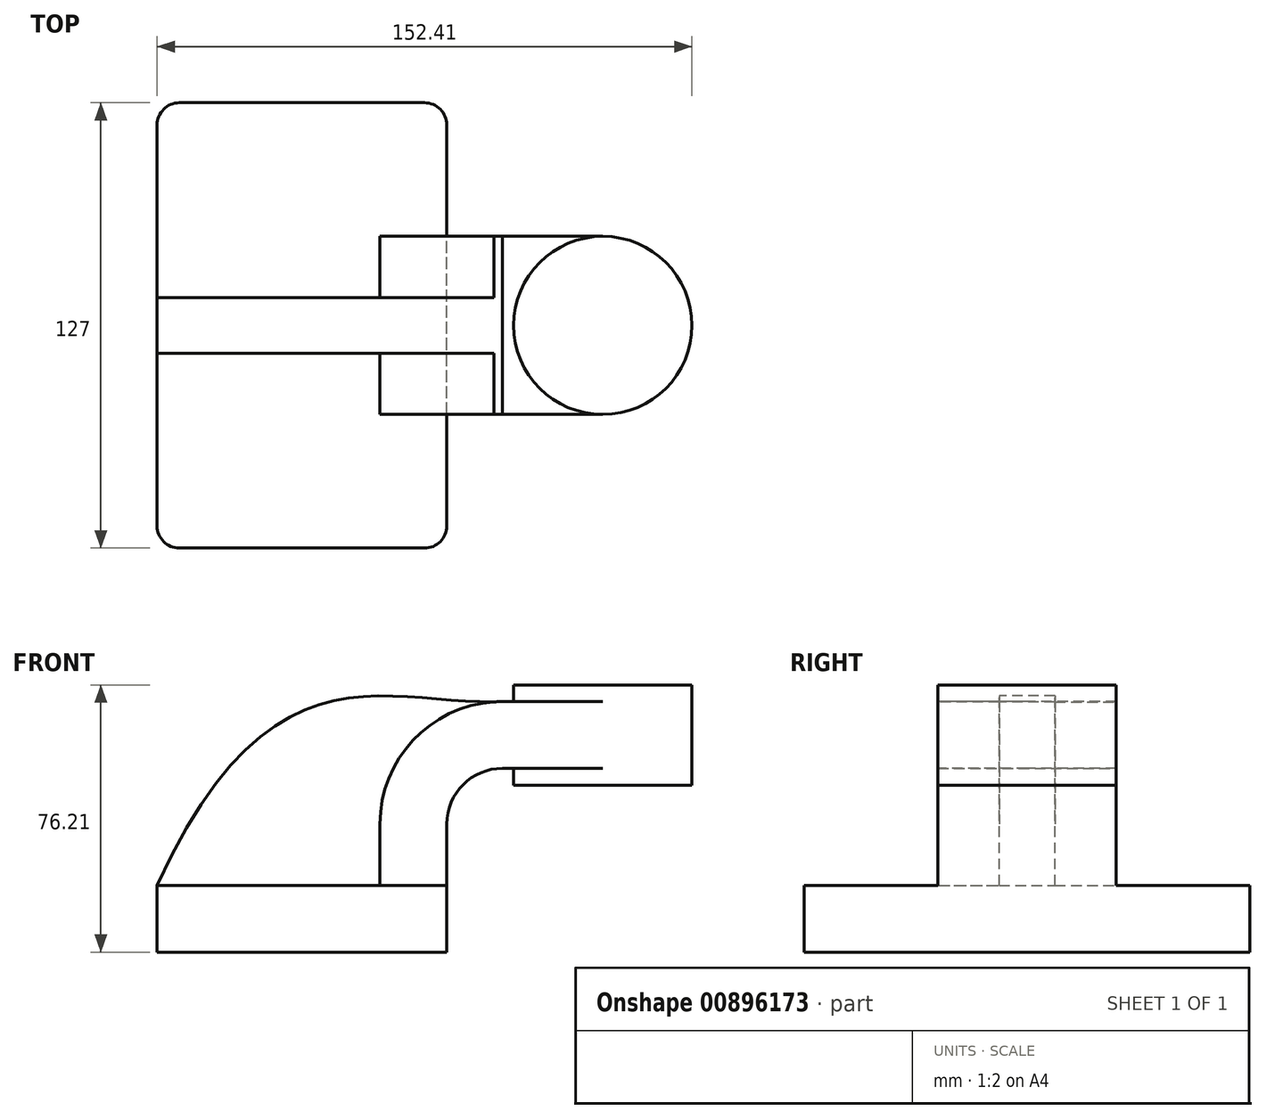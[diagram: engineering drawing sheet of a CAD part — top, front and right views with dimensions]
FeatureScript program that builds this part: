
annotation { "Feature Type Name" : "Feature", "Feature Type Description" : "" }
export const myFeature = defineFeature(function(context is Context, id is Id, definition is map)
    precondition{}
    {
        {
            var Q0;
            Q0=qCreatedBy(makeId("Front.planeOp"),FACE);
            var sketch = newSketch(context, id + "F0", { "sketchPlane" : qUnion([Q0])});
            skLineSegment(sketch, "E0.bottom", {"start": v(41.28, -9.52) * mm, "end": v(-41.28, -9.53) * mm});
            skLineSegment(sketch, "E0.top", {"start": v(41.28, 9.53) * mm, "end": v(-41.28, 9.53) * mm});
            skLineSegment(sketch, "E0.left", {"start": v(41.28, -9.52) * mm, "end": v(41.28, 9.53) * mm});
            skLineSegment(sketch, "E0.right", {"start": v(-41.28, -9.53) * mm, "end": v(-41.28, 9.53) * mm});
            skPoint(sketch, "E0.middle", {"position": v(0, 0) * mm});
            skLineSegment(sketch, "E1.bottom", {"start": v(111.12, 38.1) * mm, "end": v(60.32, 38.1) * mm});
            skLineSegment(sketch, "E1.top", {"start": v(111.13, 66.68) * mm, "end": v(60.32, 66.68) * mm});
            skLineSegment(sketch, "E1.left", {"start": v(111.13, 38.1) * mm, "end": v(111.13, 66.68) * mm});
            skLineSegment(sketch, "E1.right", {"start": v(60.32, 38.1) * mm, "end": v(60.32, 66.68) * mm});
            skPoint(sketch, "E1.middle", {"position": v(85.72, 52.39) * mm});
            skLineSegment(sketch, "E2", {"start": v(41.28, 9.53) * mm, "end": v(41.28, 27) * mm});
            skArc(sketch, "E3", {"start": v(41.27, 27) * mm, "mid": v(45.92, 38.23) * mm, "end": v(57.15, 42.88) * mm});
            skLineSegment(sketch, "E4", {"start": v(57.15, 42.88) * mm, "end": v(85.72, 42.88) * mm});
            skLineSegment(sketch, "E5.0", {"start": v(57.15, 61.93) * mm, "end": v(85.72, 61.93) * mm});
            skArc(sketch, "E5.1", {"start": v(22.23, 27) * mm, "mid": v(32.45, 51.7) * mm, "end": v(57.15, 61.93) * mm});
            skLineSegment(sketch, "E5.2", {"start": v(22.22, 9.53) * mm, "end": v(22.22, 27) * mm});
            skLineSegment(sketch, "E6", {"start": v(85.72, 38.1) * mm, "end": v(85.72, 66.68) * mm});
            skLineSegment(sketch, "E7", {"start": v(57.15, 61.93) * mm, "end": v(57.15, 61.93) * mm});
            skFitSpline(sketch, "E8", {"points": [v(-41.28, 9.52) * mm, v(57.15, 61.93) * mm], "startDerivative": vector(98.43, 215.06) * mm, "endDerivative": vector(95.36, 4.95) * mm});
            skSolve(sketch);
        }
        {
            var Q0;
            Q0=makeQuery(id+"F0.imprint","IMPRINT",FACE,{"disambiguationData":[TD([[makeQuery(id+"F0.imprint","IMPRINT",EDGE,{"derivedFrom":sQuery(id+"F0.wireOp",EDGE,"E0.bottom")}),-1.0]])]});
            extrude(context, id + "F1", {"entities" : qUnion([Q0]), "endBound" : BoundingType.SYMMETRIC, "depth" : 127 * mm, "offsetDistance" : 25.4 * mm});
        }
        {
            var Q0;
            {var subQ1=sQuery(id+"F0.wireOp",EDGE,"E2");Q0=makeQuery(id+"F0.imprint","IMPRINT",FACE,{"disambiguationData":[TD([[makeQuery(id+"F0.imprint","IMPRINT",EDGE,{"derivedFrom":subQ1}),1.0]])]});}
            var Q1;
            {var subQ0=sQuery(id+"F0.wireOp",EDGE,"E4");var subQ1=sQuery(id+"F0.wireOp",EDGE,"E1.right");var subQ2=makeQuery(id+"F0.imprint","INTERSECT",VERTEX,{"derivedFrom":[subQ1,subQ0]});Q1=makeQuery(id+"F0.imprint","IMPRINT",FACE,{"disambiguationData":[TD([[makeQuery(id+"F0.imprint","IMPRINT",EDGE,{"disambiguationData":[TD([[subQ2,-1.0]])],"derivedFrom":subQ1}),-1.0]])]});}
            extrude(context, id + "F2", {"entities" : qUnion([Q0, Q1]), "operationType" : NewBodyOperationType.ADD, "endBound" : BoundingType.SYMMETRIC, "depth" : 50.8 * mm, "offsetDistance" : 25.4 * mm});
        }
        {
            var Q0;
            {var subQ3=sQuery(id+"F0.wireOp",EDGE,"E5.2");Q0=makeQuery(id+"F0.imprint","IMPRINT",FACE,{"disambiguationData":[TD([[makeQuery(id+"F0.imprint","IMPRINT",EDGE,{"derivedFrom":subQ3}),1.0]])]});}
            extrude(context, id + "F3", {"entities" : qUnion([Q0]), "operationType" : NewBodyOperationType.ADD, "endBound" : BoundingType.SYMMETRIC, "depth" : 15.88 * mm, "offsetDistance" : 25.4 * mm});
        }
        {
            var Q0;
            {var subQ0=sQuery(id+"F0.wireOp",EDGE,"E1.left");Q0=makeQuery(id+"F0.imprint","IMPRINT",FACE,{"disambiguationData":[TD([[makeQuery(id+"F0.imprint","IMPRINT",EDGE,{"derivedFrom":subQ0}),1.0]])]});}
            var Q1;
            Q1=sQuery(id+"F0.wireOp",EDGE,"E6");
            revolve(context, id + "F4", {"operationType" : NewBodyOperationType.ADD, "surfaceOperationType" : NewSurfaceOperationType.NEW, "entities" : qUnion([Q0]), "axis" : qUnion([Q1]), "revolveType" : RevolveType.FULL});
        }
        {
            var Q0;
            Q0=makeQuery(id+"F1.opExtrude","CAP_EDGE",EDGE,{"disambiguationData":[OSD([sQuery(id+"F0.wireOp",EDGE,"E0.left")])],"isStart":false});
            var Q1;
            Q1=makeQuery(id+"F1.opExtrude","CAP_EDGE",EDGE,{"disambiguationData":[OSD([sQuery(id+"F0.wireOp",EDGE,"E0.right")])],"isStart":false});
            var Q2;
            Q2=makeQuery(id+"F1.opExtrude","CAP_EDGE",EDGE,{"disambiguationData":[OSD([sQuery(id+"F0.wireOp",EDGE,"E0.right")])],"isStart":true});
            var Q3;
            Q3=makeQuery(id+"F1.opExtrude","CAP_EDGE",EDGE,{"disambiguationData":[OSD([sQuery(id+"F0.wireOp",EDGE,"E0.left")])],"isStart":true});
            fillet(context, id + "F5", {"entities" : qUnion([Q0, Q1, Q2, Q3]), "radius" : 6.35 * mm, "tangentPropagation" : true, "allowEdgeOverflow" : false});
        }
    });
